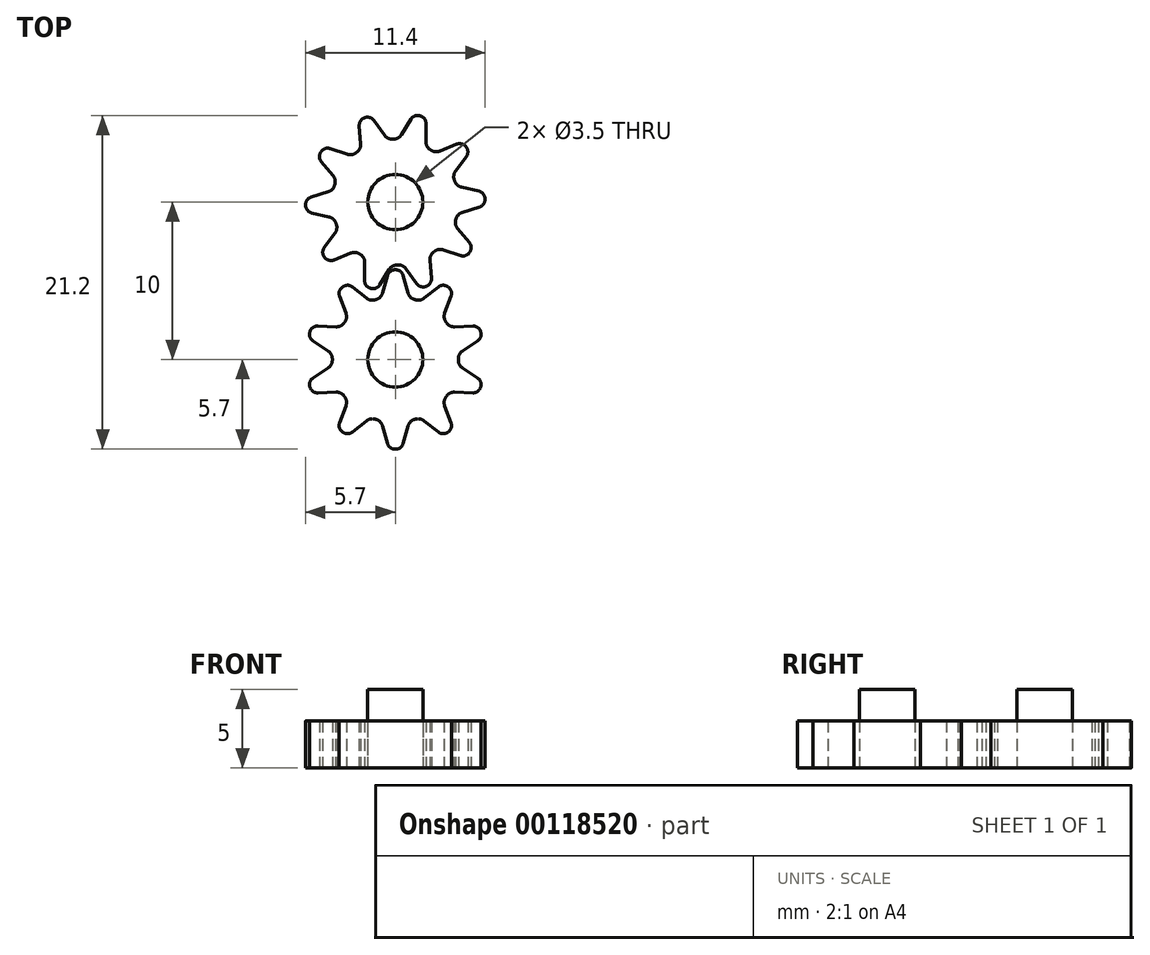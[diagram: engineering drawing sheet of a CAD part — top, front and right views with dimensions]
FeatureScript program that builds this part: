
annotation { "Feature Type Name" : "Feature", "Feature Type Description" : "" }
export const myFeature = defineFeature(function(context is Context, id is Id, definition is map)
    precondition{}
    {
        {
            var Q0;
            Q0=qCreatedBy(makeId("Top.planeOp"),FACE);
            var sketch = newSketch(context, id + "F0", { "sketchPlane" : qUnion([Q0])});
            skCircle(sketch, "E0", {"center": v(0, 0) * mm, "radius": 5 * mm, "construction": true});
            skLineSegment(sketch, "E1", {"start": v(0, 4) * mm, "end": v(0, 5.7) * mm, "construction": true});
            skArc(sketch, "E2", {"start": v(0.4, 5.69) * mm, "mid": v(0, 5.7) * mm, "end": v(-0.4, 5.69) * mm});
            skArc(sketch, "E3", {"start": v(-0.9, 3.9) * mm, "mid": v(0, -4) * mm, "end": v(0.9, 3.9) * mm});
            skLineSegment(sketch, "E4", {"start": v(0.4, 5.69) * mm, "end": v(0.9, 3.9) * mm});
            skLineSegment(sketch, "E5", {"start": v(-0.9, 3.9) * mm, "end": v(-0.4, 5.69) * mm});
            skPoint(sketch, "E6", {"position": v(0, 5) * mm});
            skLineSegment(sketch, "E7.1.0", {"start": v(-3.02, 4.84) * mm, "end": v(-1.56, 3.68) * mm});
            skPoint(sketch, "E7.1.1", {"position": v(-2.94, 4.05) * mm});
            skLineSegment(sketch, "E7.1.2", {"start": v(-3.02, 2.62) * mm, "end": v(-3.67, 4.36) * mm});
            skArc(sketch, "E7.1.3", {"start": v(-3.02, 4.84) * mm, "mid": v(-3.35, 4.61) * mm, "end": v(-3.67, 4.36) * mm});
            skLineSegment(sketch, "E7.1.4", {"start": v(-2.35, 3.24) * mm, "end": v(-3.35, 4.61) * mm, "construction": true});
            skLineSegment(sketch, "E7.2.0", {"start": v(-5.28, 2.14) * mm, "end": v(-3.43, 2.06) * mm});
            skPoint(sketch, "E7.2.1", {"position": v(-4.76, 1.55) * mm});
            skLineSegment(sketch, "E7.2.2", {"start": v(-3.98, 0.35) * mm, "end": v(-5.53, 1.38) * mm});
            skArc(sketch, "E7.2.3", {"start": v(-5.28, 2.14) * mm, "mid": v(-5.42, 1.76) * mm, "end": v(-5.53, 1.38) * mm});
            skLineSegment(sketch, "E7.2.4", {"start": v(-3.8, 1.24) * mm, "end": v(-5.42, 1.76) * mm, "construction": true});
            skLineSegment(sketch, "E7.3.0", {"start": v(-5.53, -1.38) * mm, "end": v(-3.98, -0.35) * mm});
            skPoint(sketch, "E7.3.1", {"position": v(-4.76, -1.55) * mm});
            skLineSegment(sketch, "E7.3.2", {"start": v(-3.43, -2.06) * mm, "end": v(-5.28, -2.14) * mm});
            skArc(sketch, "E7.3.3", {"start": v(-5.53, -1.38) * mm, "mid": v(-5.42, -1.76) * mm, "end": v(-5.28, -2.14) * mm});
            skLineSegment(sketch, "E7.3.4", {"start": v(-3.8, -1.24) * mm, "end": v(-5.42, -1.76) * mm, "construction": true});
            skLineSegment(sketch, "E7.4.0", {"start": v(-3.67, -4.36) * mm, "end": v(-3.02, -2.62) * mm});
            skPoint(sketch, "E7.4.1", {"position": v(-2.94, -4.05) * mm});
            skLineSegment(sketch, "E7.4.2", {"start": v(-1.56, -3.68) * mm, "end": v(-3.02, -4.84) * mm});
            skArc(sketch, "E7.4.3", {"start": v(-3.67, -4.36) * mm, "mid": v(-3.35, -4.61) * mm, "end": v(-3.02, -4.84) * mm});
            skLineSegment(sketch, "E7.4.4", {"start": v(-2.35, -3.24) * mm, "end": v(-3.35, -4.61) * mm, "construction": true});
            skLineSegment(sketch, "E7.5.0", {"start": v(-0.4, -5.69) * mm, "end": v(-0.9, -3.9) * mm});
            skPoint(sketch, "E7.5.1", {"position": v(0, -5) * mm});
            skLineSegment(sketch, "E7.5.2", {"start": v(0.9, -3.9) * mm, "end": v(0.4, -5.69) * mm});
            skArc(sketch, "E7.5.3", {"start": v(-0.4, -5.69) * mm, "mid": v(0, -5.7) * mm, "end": v(0.4, -5.69) * mm});
            skLineSegment(sketch, "E7.5.4", {"start": v(0, -4) * mm, "end": v(0, -5.7) * mm, "construction": true});
            skLineSegment(sketch, "E7.6.0", {"start": v(3.02, -4.84) * mm, "end": v(1.56, -3.68) * mm});
            skPoint(sketch, "E7.6.1", {"position": v(2.94, -4.05) * mm});
            skLineSegment(sketch, "E7.6.2", {"start": v(3.02, -2.62) * mm, "end": v(3.67, -4.36) * mm});
            skArc(sketch, "E7.6.3", {"start": v(3.02, -4.84) * mm, "mid": v(3.35, -4.61) * mm, "end": v(3.67, -4.36) * mm});
            skLineSegment(sketch, "E7.6.4", {"start": v(2.35, -3.24) * mm, "end": v(3.35, -4.61) * mm, "construction": true});
            skLineSegment(sketch, "E7.7.0", {"start": v(5.28, -2.14) * mm, "end": v(3.43, -2.06) * mm});
            skPoint(sketch, "E7.7.1", {"position": v(4.76, -1.55) * mm});
            skLineSegment(sketch, "E7.7.2", {"start": v(3.98, -0.35) * mm, "end": v(5.53, -1.38) * mm});
            skArc(sketch, "E7.7.3", {"start": v(5.28, -2.14) * mm, "mid": v(5.42, -1.76) * mm, "end": v(5.53, -1.38) * mm});
            skLineSegment(sketch, "E7.7.4", {"start": v(3.8, -1.24) * mm, "end": v(5.42, -1.76) * mm, "construction": true});
            skCircle(sketch, "E8", {"center": v(0, 0) * mm, "radius": 1.75 * mm});
            skLineSegment(sketch, "E9.2.8.0", {"start": v(5.53, 1.38) * mm, "end": v(3.98, 0.35) * mm});
            skPoint(sketch, "E9.3.8.0", {"position": v(4.76, 1.55) * mm});
            skLineSegment(sketch, "E9.4.8.0", {"start": v(3.43, 2.06) * mm, "end": v(5.28, 2.14) * mm});
            skArc(sketch, "E9.7.8.0", {"start": v(5.53, 1.38) * mm, "mid": v(5.42, 1.76) * mm, "end": v(5.28, 2.14) * mm});
            skLineSegment(sketch, "E9.11.8.0", {"start": v(3.8, 1.24) * mm, "end": v(5.42, 1.76) * mm, "construction": true});
            skLineSegment(sketch, "E10.2.9.0", {"start": v(3.67, 4.36) * mm, "end": v(3.02, 2.62) * mm});
            skPoint(sketch, "E10.3.9.0", {"position": v(2.94, 4.05) * mm});
            skLineSegment(sketch, "E10.4.9.0", {"start": v(1.56, 3.68) * mm, "end": v(3.02, 4.84) * mm});
            skArc(sketch, "E10.7.9.0", {"start": v(3.67, 4.36) * mm, "mid": v(3.35, 4.61) * mm, "end": v(3.02, 4.84) * mm});
            skLineSegment(sketch, "E10.11.9.0", {"start": v(2.35, 3.24) * mm, "end": v(3.35, 4.61) * mm, "construction": true});
            skSolve(sketch);
        }
        {
            var Q0;
            Q0=qSketchRegion(id+"F0",true);
            extrude(context, id + "F1", {"entities" : qUnion([Q0]), "depth" : 3 * mm});
        }
        {
            var Q0;
            Q0=makeQuery(id+"F1.opExtrude","SWEPT_EDGE",EDGE,{"disambiguationData":[OSD([sQuery(id+"F0.wireOp",EDGE,"E2"),sQuery(id+"F0.wireOp",EDGE,"E4")])]});
            var Q1;
            Q1=makeQuery(id+"F1.opExtrude","SWEPT_EDGE",EDGE,{"disambiguationData":[OSD([sQuery(id+"F0.wireOp",EDGE,"E2"),sQuery(id+"F0.wireOp",EDGE,"E5")])]});
            var Q2;
            Q2=makeQuery(id+"F1.opExtrude","SWEPT_EDGE",EDGE,{"disambiguationData":[OSD([sQuery(id+"F0.wireOp",EDGE,"E7.1.0"),sQuery(id+"F0.wireOp",EDGE,"E7.1.3")])]});
            var Q3;
            Q3=makeQuery(id+"F1.opExtrude","SWEPT_EDGE",EDGE,{"disambiguationData":[OSD([sQuery(id+"F0.wireOp",EDGE,"E7.1.2"),sQuery(id+"F0.wireOp",EDGE,"E7.1.3")])]});
            var Q4;
            Q4=makeQuery(id+"F1.opExtrude","SWEPT_EDGE",EDGE,{"disambiguationData":[OSD([sQuery(id+"F0.wireOp",EDGE,"E9.4.8.0"),sQuery(id+"F0.wireOp",EDGE,"E9.7.8.0")])]});
            var Q5;
            Q5=makeQuery(id+"F1.opExtrude","SWEPT_EDGE",EDGE,{"disambiguationData":[OSD([sQuery(id+"F0.wireOp",EDGE,"E9.2.8.0"),sQuery(id+"F0.wireOp",EDGE,"E9.7.8.0")])]});
            var Q6;
            Q6=makeQuery(id+"F1.opExtrude","SWEPT_EDGE",EDGE,{"disambiguationData":[OSD([sQuery(id+"F0.wireOp",EDGE,"E7.7.2"),sQuery(id+"F0.wireOp",EDGE,"E7.7.3")])]});
            var Q7;
            Q7=makeQuery(id+"F1.opExtrude","SWEPT_EDGE",EDGE,{"disambiguationData":[OSD([sQuery(id+"F0.wireOp",EDGE,"E7.2.0"),sQuery(id+"F0.wireOp",EDGE,"E7.2.3")])]});
            var Q8;
            Q8=makeQuery(id+"F1.opExtrude","SWEPT_EDGE",EDGE,{"disambiguationData":[OSD([sQuery(id+"F0.wireOp",EDGE,"E7.7.0"),sQuery(id+"F0.wireOp",EDGE,"E7.7.3")])]});
            var Q9;
            Q9=makeQuery(id+"F1.opExtrude","SWEPT_EDGE",EDGE,{"disambiguationData":[OSD([sQuery(id+"F0.wireOp",EDGE,"E7.6.2"),sQuery(id+"F0.wireOp",EDGE,"E7.6.3")])]});
            var Q10;
            Q10=makeQuery(id+"F1.opExtrude","SWEPT_EDGE",EDGE,{"disambiguationData":[OSD([sQuery(id+"F0.wireOp",EDGE,"E7.6.0"),sQuery(id+"F0.wireOp",EDGE,"E7.6.3")])]});
            var Q11;
            Q11=makeQuery(id+"F1.opExtrude","SWEPT_EDGE",EDGE,{"disambiguationData":[OSD([sQuery(id+"F0.wireOp",EDGE,"E7.5.2"),sQuery(id+"F0.wireOp",EDGE,"E7.5.3")])]});
            var Q12;
            Q12=makeQuery(id+"F1.opExtrude","SWEPT_EDGE",EDGE,{"disambiguationData":[OSD([sQuery(id+"F0.wireOp",EDGE,"E7.5.0"),sQuery(id+"F0.wireOp",EDGE,"E7.5.3")])]});
            var Q13;
            Q13=makeQuery(id+"F1.opExtrude","SWEPT_EDGE",EDGE,{"disambiguationData":[OSD([sQuery(id+"F0.wireOp",EDGE,"E7.4.2"),sQuery(id+"F0.wireOp",EDGE,"E7.4.3")])]});
            var Q14;
            Q14=makeQuery(id+"F1.opExtrude","SWEPT_EDGE",EDGE,{"disambiguationData":[OSD([sQuery(id+"F0.wireOp",EDGE,"E7.4.0"),sQuery(id+"F0.wireOp",EDGE,"E7.4.3")])]});
            var Q15;
            Q15=makeQuery(id+"F1.opExtrude","SWEPT_EDGE",EDGE,{"disambiguationData":[OSD([sQuery(id+"F0.wireOp",EDGE,"E7.3.2"),sQuery(id+"F0.wireOp",EDGE,"E7.3.3")])]});
            var Q16;
            Q16=makeQuery(id+"F1.opExtrude","SWEPT_EDGE",EDGE,{"disambiguationData":[OSD([sQuery(id+"F0.wireOp",EDGE,"E7.3.0"),sQuery(id+"F0.wireOp",EDGE,"E7.3.3")])]});
            var Q17;
            Q17=makeQuery(id+"F1.opExtrude","SWEPT_EDGE",EDGE,{"disambiguationData":[OSD([sQuery(id+"F0.wireOp",EDGE,"E7.2.2"),sQuery(id+"F0.wireOp",EDGE,"E7.2.3")])]});
            var Q18;
            Q18=makeQuery(id+"F1.opExtrude","SWEPT_EDGE",EDGE,{"disambiguationData":[OSD([sQuery(id+"F0.wireOp",EDGE,"E10.2.9.0"),sQuery(id+"F0.wireOp",EDGE,"E10.7.9.0")])]});
            var Q19;
            Q19=makeQuery(id+"F1.opExtrude","SWEPT_EDGE",EDGE,{"disambiguationData":[OSD([sQuery(id+"F0.wireOp",EDGE,"E10.4.9.0"),sQuery(id+"F0.wireOp",EDGE,"E10.7.9.0")])]});
            fillet(context, id + "F2", {"entities" : qUnion([Q0, Q1, Q2, Q3, Q4, Q5, Q6, Q7, Q8, Q9, Q10, Q11, Q12, Q13, Q14, Q15, Q16, Q17, Q18, Q19]), "radius" : 0.5 * mm, "tangentPropagation" : true, "allowEdgeOverflow" : false});
        }
        {
            var Q0;
            Q0=makeQuery(id+"F1.opExtrude","SWEPT_EDGE",EDGE,{"disambiguationData":[OSD([sQuery(id+"F0.wireOp",EDGE,"E3"),sQuery(id+"F0.wireOp",EDGE,"E7.1.0")])]});
            var Q1;
            Q1=makeQuery(id+"F1.opExtrude","SWEPT_EDGE",EDGE,{"disambiguationData":[OSD([sQuery(id+"F0.wireOp",EDGE,"E3"),sQuery(id+"F0.wireOp",EDGE,"E4")])]});
            var Q2;
            Q2=makeQuery(id+"F1.opExtrude","SWEPT_EDGE",EDGE,{"disambiguationData":[OSD([sQuery(id+"F0.wireOp",EDGE,"E3"),sQuery(id+"F0.wireOp",EDGE,"E10.4.9.0")])]});
            var Q3;
            Q3=makeQuery(id+"F1.opExtrude","SWEPT_EDGE",EDGE,{"disambiguationData":[OSD([sQuery(id+"F0.wireOp",EDGE,"E3"),sQuery(id+"F0.wireOp",EDGE,"E5")])]});
            var Q4;
            Q4=makeQuery(id+"F1.opExtrude","SWEPT_EDGE",EDGE,{"disambiguationData":[OSD([sQuery(id+"F0.wireOp",EDGE,"E3"),sQuery(id+"F0.wireOp",EDGE,"E7.2.0")])]});
            var Q5;
            Q5=makeQuery(id+"F1.opExtrude","SWEPT_EDGE",EDGE,{"disambiguationData":[OSD([sQuery(id+"F0.wireOp",EDGE,"E3"),sQuery(id+"F0.wireOp",EDGE,"E7.1.2")])]});
            var Q6;
            Q6=makeQuery(id+"F1.opExtrude","SWEPT_EDGE",EDGE,{"disambiguationData":[OSD([sQuery(id+"F0.wireOp",EDGE,"E3"),sQuery(id+"F0.wireOp",EDGE,"E10.2.9.0")])]});
            var Q7;
            Q7=makeQuery(id+"F1.opExtrude","SWEPT_EDGE",EDGE,{"disambiguationData":[OSD([sQuery(id+"F0.wireOp",EDGE,"E3"),sQuery(id+"F0.wireOp",EDGE,"E9.4.8.0")])]});
            var Q8;
            Q8=makeQuery(id+"F1.opExtrude","SWEPT_EDGE",EDGE,{"disambiguationData":[OSD([sQuery(id+"F0.wireOp",EDGE,"E3"),sQuery(id+"F0.wireOp",EDGE,"E7.7.2")])]});
            var Q9;
            Q9=makeQuery(id+"F1.opExtrude","SWEPT_EDGE",EDGE,{"disambiguationData":[OSD([sQuery(id+"F0.wireOp",EDGE,"E3"),sQuery(id+"F0.wireOp",EDGE,"E9.2.8.0")])]});
            var Q10;
            Q10=makeQuery(id+"F1.opExtrude","SWEPT_EDGE",EDGE,{"disambiguationData":[OSD([sQuery(id+"F0.wireOp",EDGE,"E3"),sQuery(id+"F0.wireOp",EDGE,"E7.6.2")])]});
            var Q11;
            Q11=makeQuery(id+"F1.opExtrude","SWEPT_EDGE",EDGE,{"disambiguationData":[OSD([sQuery(id+"F0.wireOp",EDGE,"E3"),sQuery(id+"F0.wireOp",EDGE,"E7.7.0")])]});
            var Q12;
            Q12=makeQuery(id+"F1.opExtrude","SWEPT_EDGE",EDGE,{"disambiguationData":[OSD([sQuery(id+"F0.wireOp",EDGE,"E3"),sQuery(id+"F0.wireOp",EDGE,"E7.5.2")])]});
            var Q13;
            Q13=makeQuery(id+"F1.opExtrude","SWEPT_EDGE",EDGE,{"disambiguationData":[OSD([sQuery(id+"F0.wireOp",EDGE,"E3"),sQuery(id+"F0.wireOp",EDGE,"E7.6.0")])]});
            var Q14;
            Q14=makeQuery(id+"F1.opExtrude","SWEPT_EDGE",EDGE,{"disambiguationData":[OSD([sQuery(id+"F0.wireOp",EDGE,"E3"),sQuery(id+"F0.wireOp",EDGE,"E7.5.0")])]});
            var Q15;
            Q15=makeQuery(id+"F1.opExtrude","SWEPT_EDGE",EDGE,{"disambiguationData":[OSD([sQuery(id+"F0.wireOp",EDGE,"E3"),sQuery(id+"F0.wireOp",EDGE,"E7.4.2")])]});
            var Q16;
            Q16=makeQuery(id+"F1.opExtrude","SWEPT_EDGE",EDGE,{"disambiguationData":[OSD([sQuery(id+"F0.wireOp",EDGE,"E3"),sQuery(id+"F0.wireOp",EDGE,"E7.4.0")])]});
            var Q17;
            Q17=makeQuery(id+"F1.opExtrude","SWEPT_EDGE",EDGE,{"disambiguationData":[OSD([sQuery(id+"F0.wireOp",EDGE,"E3"),sQuery(id+"F0.wireOp",EDGE,"E7.3.2")])]});
            var Q18;
            Q18=makeQuery(id+"F1.opExtrude","SWEPT_EDGE",EDGE,{"disambiguationData":[OSD([sQuery(id+"F0.wireOp",EDGE,"E3"),sQuery(id+"F0.wireOp",EDGE,"E7.3.0")])]});
            var Q19;
            Q19=makeQuery(id+"F1.opExtrude","SWEPT_EDGE",EDGE,{"disambiguationData":[OSD([sQuery(id+"F0.wireOp",EDGE,"E3"),sQuery(id+"F0.wireOp",EDGE,"E7.2.2")])]});
            fillet(context, id + "F3", {"entities" : qUnion([Q0, Q1, Q2, Q3, Q4, Q5, Q6, Q7, Q8, Q9, Q10, Q11, Q12, Q13, Q14, Q15, Q16, Q17, Q18, Q19]), "radius" : 0.6 * mm, "tangentPropagation" : true, "allowEdgeOverflow" : false});
        }
        {
            var Q0;
            Q0=qCreatedBy(makeId("Right.planeOp"),FACE);
            var sketch = newSketch(context, id + "F4", { "sketchPlane" : qUnion([Q0])});
            skLineSegment(sketch, "E11", {"start": v(0, 0) * mm, "end": v(0, 14.37) * mm, "construction": true});
            skSolve(sketch);
        }
        {
            var Q0;
            Q0=makeQuery(id+"F1.opExtrude","SWEPT_BODY",BODY,{"disambiguationData":[OSD([sQuery(id+"F0.wireOp",EDGE,"E2"),sQuery(id+"F0.wireOp",EDGE,"E3"),sQuery(id+"F0.wireOp",EDGE,"E4"),sQuery(id+"F0.wireOp",EDGE,"E5")])]});
            var Q1;
            Q1=sQuery(id+"F4.wireOp",EDGE,"E11");
            transform(context, id + "F5", {"entities" : qUnion([Q0]), "transformType" : TransformType.ROTATION, "transformAxis" : qUnion([Q1]), "angle" : 200 * degree, "makeCopy" : true});
        }
        {
            var Q0;
            Q0=makeQuery(id+"F5.opPattern","COPY",BODY,{"derivedFrom":makeQuery(id+"F1.opExtrude","SWEPT_BODY",BODY,{"disambiguationData":[OSD([sQuery(id+"F0.wireOp",EDGE,"E2"),sQuery(id+"F0.wireOp",EDGE,"E3"),sQuery(id+"F0.wireOp",EDGE,"E4"),sQuery(id+"F0.wireOp",EDGE,"E5")])]}),"instanceName":"1"});
            transform(context, id + "F6", {"entities" : qUnion([Q0]), "transformType" : TransformType.TRANSLATION_3D, "dx" : 0 * mm, "dy" : 10 * mm, "dz" : 0 * mm, "makeCopy" : false});
        }
        {
            var Q0;
            Q0=qCreatedBy(makeId("Top.planeOp"),FACE);
            var sketch = newSketch(context, id + "F7", { "sketchPlane" : qUnion([Q0])});
            skCircle(sketch, "E12", {"center": v(0, 0) * mm, "radius": 1.75 * mm});
            skCircle(sketch, "E13", {"center": v(0, 10) * mm, "radius": 1.75 * mm});
            skSolve(sketch);
        }
        {
            var Q0;
            Q0=qSketchRegion(id+"F7",true);
            extrude(context, id + "F8", {"entities" : qUnion([Q0]), "depth" : 5 * mm});
        }
    });
